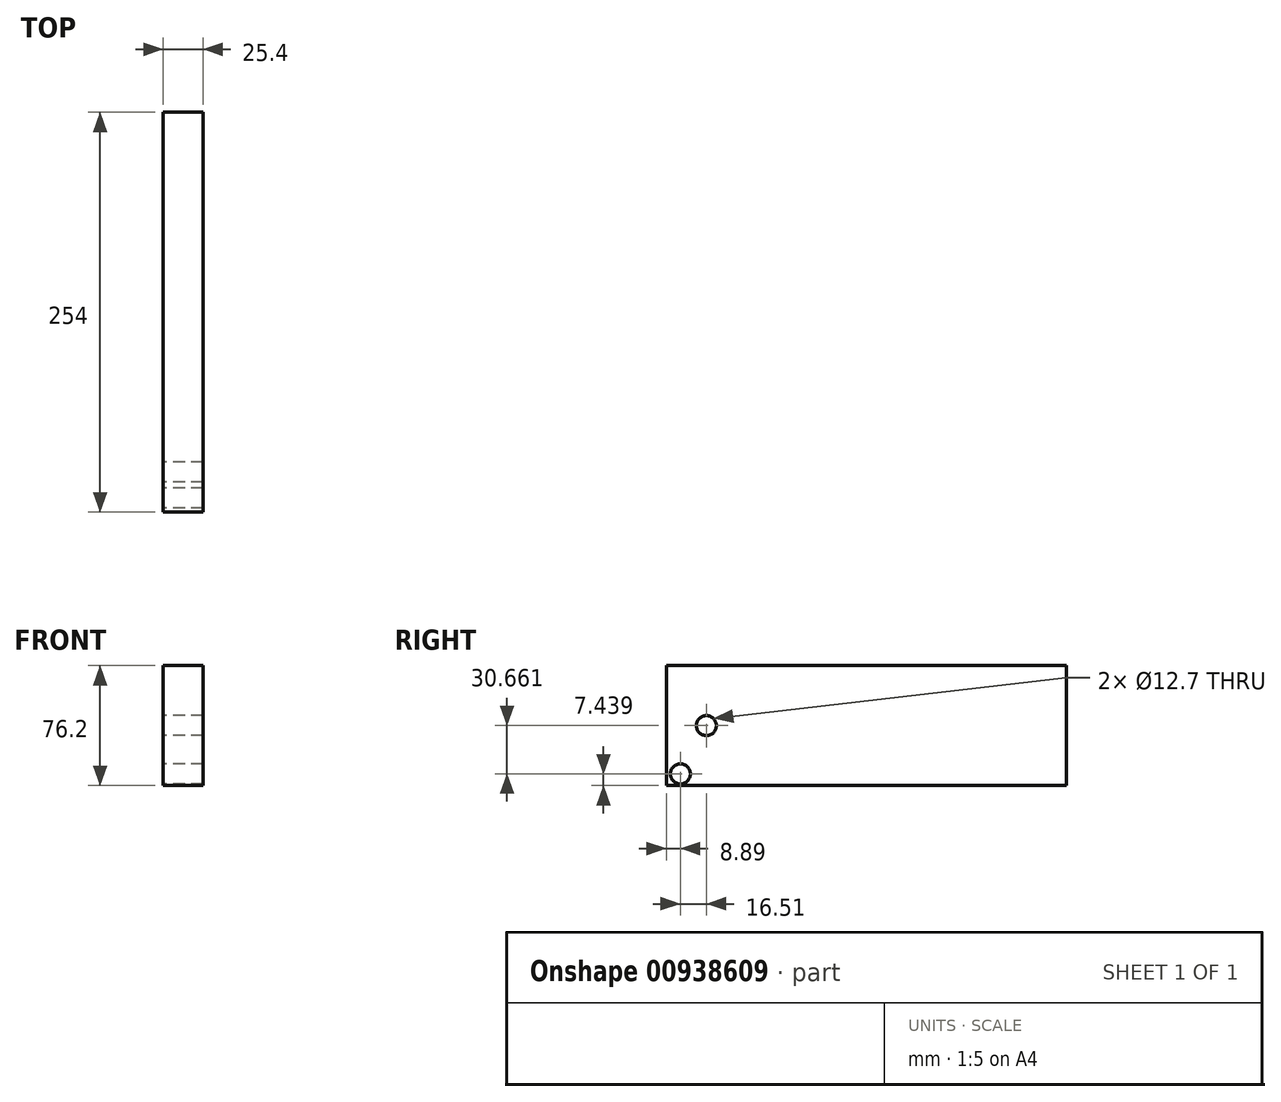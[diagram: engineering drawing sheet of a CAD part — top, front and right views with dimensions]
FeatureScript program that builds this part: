
annotation { "Feature Type Name" : "Feature", "Feature Type Description" : "" }
export const myFeature = defineFeature(function(context is Context, id is Id, definition is map)
    precondition{}
    {
        {
            var Q0;
            Q0=qCreatedBy(makeId("Right.planeOp"),FACE);
            var sketch = newSketch(context, id + "F0", { "sketchPlane" : qUnion([Q0])});
            skLineSegment(sketch, "E0.bottom", {"start": v(-127, 38.1) * mm, "end": v(127, 38.1) * mm});
            skLineSegment(sketch, "E0.top", {"start": v(-127, -38.1) * mm, "end": v(127, -38.1) * mm});
            skLineSegment(sketch, "E0.left", {"start": v(-127, 38.1) * mm, "end": v(-127, -38.1) * mm});
            skLineSegment(sketch, "E0.right", {"start": v(127, 38.1) * mm, "end": v(127, -38.1) * mm});
            skPoint(sketch, "E0.middle", {"position": v(0, 0) * mm});
            skCircle(sketch, "E1", {"center": v(-101.6, 0) * mm, "radius": 6.35 * mm});
            skCircle(sketch, "E2", {"center": v(-118.11, -30.66) * mm, "radius": 6.35 * mm});
            skSolve(sketch);
        }
        {
            var Q0;
            Q0=makeQuery(id+"F0.imprint","IMPRINT",FACE,{"disambiguationData":[TD([[makeQuery(id+"F0.imprint","IMPRINT",EDGE,{"derivedFrom":sQuery(id+"F0.wireOp",EDGE,"E0.bottom")}),-1.0]])]});
            extrude(context, id + "F1", {"entities" : qUnion([Q0]), "depth" : 25.4 * mm, "offsetDistance" : 25.4 * mm});
        }
    });
